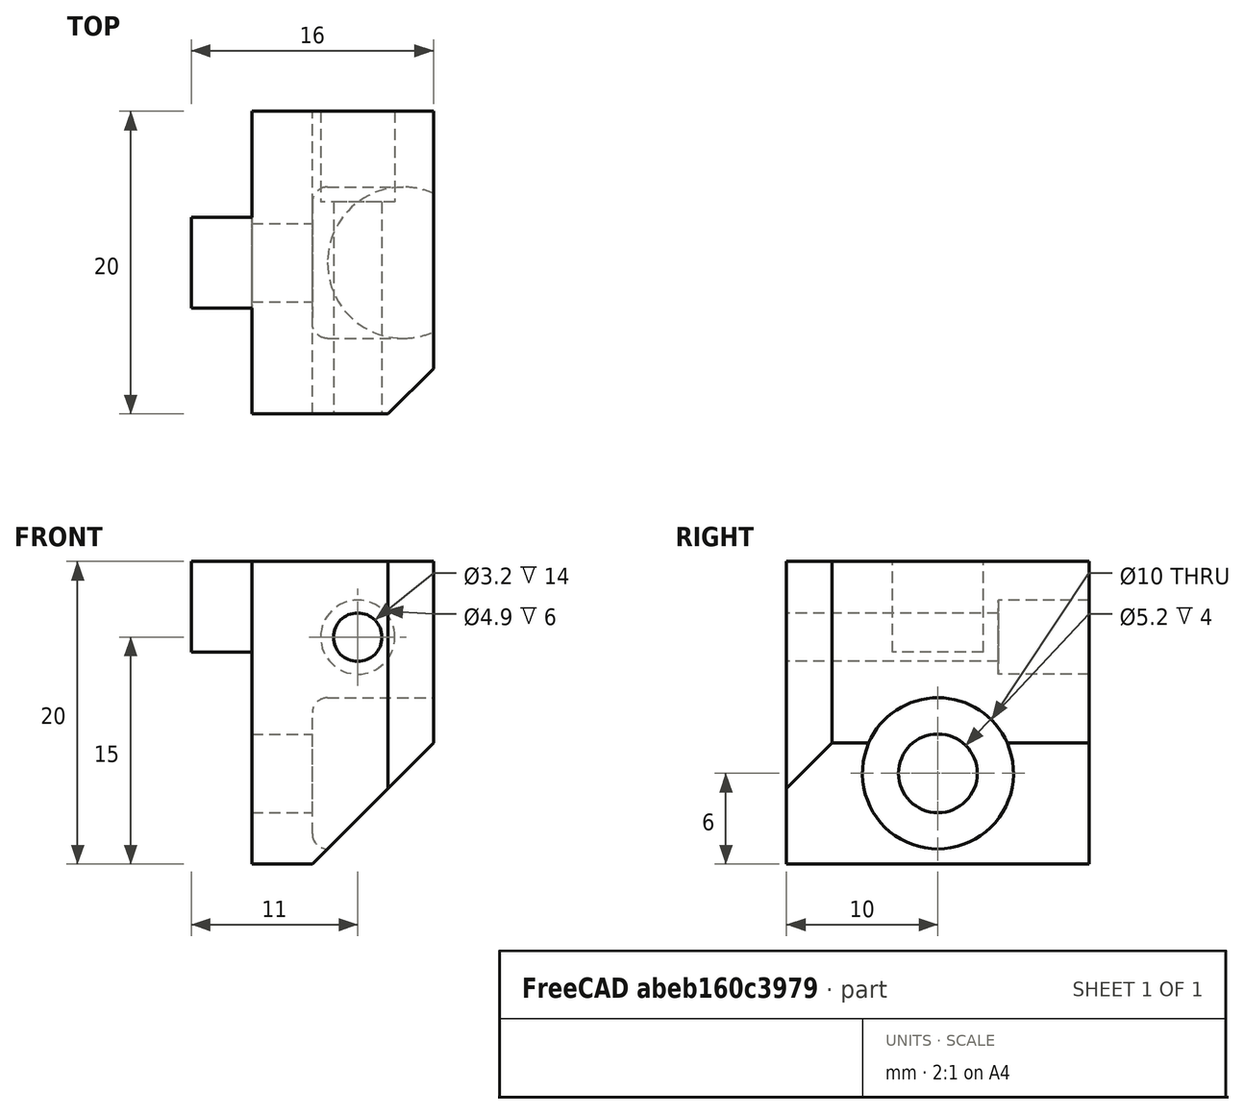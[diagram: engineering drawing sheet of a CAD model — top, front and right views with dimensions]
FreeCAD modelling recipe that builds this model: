
FCSTD DOCUMENT  (FreeCAD 0.18R)
Label: Adaptador
License: All rights reserved
LicenseURL: http://en.wikipedia.org/wiki/All_rights_reserved
objects: Part::Cylinder×4, Part::Cut×4, Part::Box×2, Part::Chamfer×2, Part::MultiFuse×1, Part::Fillet×1
note: 14 computed .brp shape members not serialized (recipe doc carries the construction recipe); baked Part::Feature solids carry a one-line shape summary decoded from their .brp

FEATURE [Part::Box] Box  label="Cubo"
  AttacherType = Attacher::AttachEngine3D
  Height = 20
  Length = 12
  Width = 20
FEATURE [Part::Box] Box001  label="Cubo001"
  AttacherType = Attacher::AttachEngine3D
  Height = 6
  Length = 10
  Placement = pos=(-4,7,14) rot=(0,0,1;0rad)
  Width = 6
FEATURE [Part::Cylinder] Cylinder  label="Cilindro"
  Angle = 360
  AttacherType = Attacher::AttachEngine3D
  Height = 30
  Placement = pos=(7,44,15) rot=(1,0,0;1.5708rad)
  Radius = 2.45
FEATURE [Part::Cylinder] Cylinder001  label="Cilindro001"
  Angle = 360
  AttacherType = Attacher::AttachEngine3D
  Height = 16
  Placement = pos=(6,10,6) rot=(0,1,0;1.5708rad)
  Radius = 5
FEATURE [Part::Cylinder] Cylinder002  label="Cilindro002"
  Angle = 360
  AttacherType = Attacher::AttachEngine3D
  Height = 20
  Placement = pos=(-9,10,6) rot=(0,1,0;1.5708rad)
  Radius = 2.6
FEATURE [Part::Cylinder] Cylinder003  label="Cilindro003"
  Angle = 360
  AttacherType = Attacher::AttachEngine3D
  Height = 28
  Placement = pos=(7,23,15) rot=(1,0,0;1.5708rad)
  Radius = 1.6
FEATURE [Part::MultiFuse] Fusion
  Shapes = -> [Box,Box001]
FEATURE [Part::Cut] Cut
  Base = -> Fusion
  Tool = -> Cylinder
FEATURE [Part::Cut] Cut001
  Base = -> Cut
  Tool = -> Cylinder003
FEATURE [Part::Chamfer] Chamfer
  Base = -> Cut001
  Edges = 1 edges r=8: [Edge25]
  Placement = pos=(-2,0,0) rot=(0,0,1;0rad)
FEATURE [Part::Fillet] Fillet
  Base = -> Cylinder001
  Edges = 1 edges r=1: [Edge3]
  Placement = pos=(-4,0,0) rot=(0,0,1;0rad)
FEATURE [Part::Cut] Cut002
  Base = -> Chamfer
  Tool = -> Fillet
FEATURE [Part::Cut] Cut003
  Base = -> Cut002
  Tool = -> Cylinder002
FEATURE [Part::Chamfer] Chamfer001
  Base = -> Cut003
  Edges = 1 edges r=3: [Edge22]
